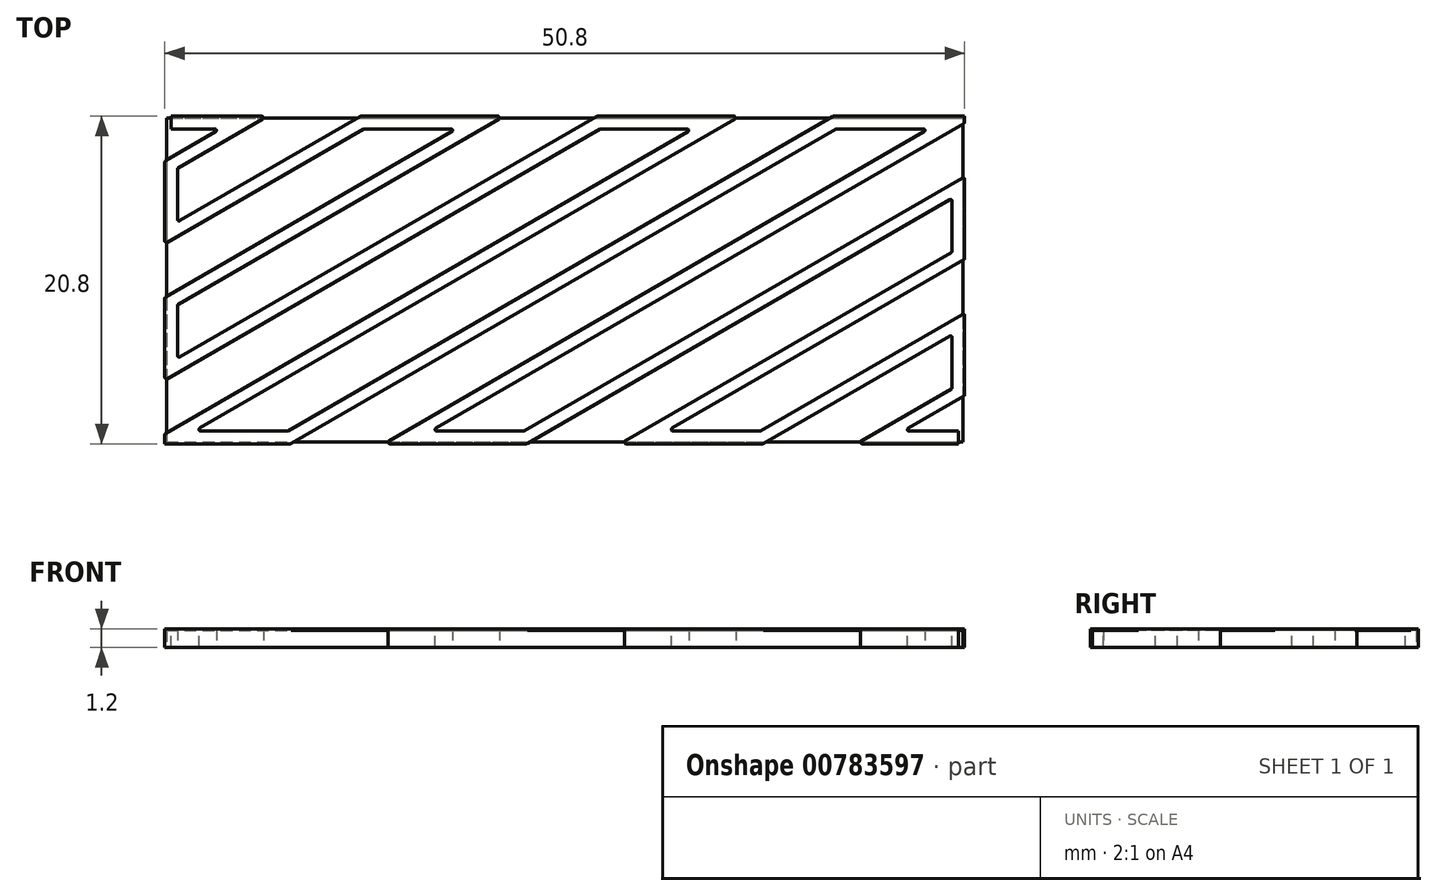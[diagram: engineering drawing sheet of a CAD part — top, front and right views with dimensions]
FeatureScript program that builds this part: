
annotation { "Feature Type Name" : "Feature", "Feature Type Description" : "" }
export const myFeature = defineFeature(function(context is Context, id is Id, definition is map)
    precondition{}
    {
        {
            var Q0;
            Q0=qCreatedBy(makeId("Top.planeOp"),FACE);
            var sketch = newSketch(context, id + "F0", { "sketchPlane" : qUnion([Q0])});
            skLineSegment(sketch, "E0.bottom", {"start": v(0, 0) * mm, "end": v(50, 0) * mm});
            skLineSegment(sketch, "E0.top", {"start": v(0, 20) * mm, "end": v(50, 20) * mm});
            skLineSegment(sketch, "E0.left", {"start": v(0, 0) * mm, "end": v(0, 20) * mm});
            skLineSegment(sketch, "E0.right", {"start": v(50, 0) * mm, "end": v(50, 20) * mm});
            skSolve(sketch);
        }
        {
            var Q0;
            Q0=qCreatedBy(makeId("Top.planeOp"),FACE);
            var sketch = newSketch(context, id + "F1", { "sketchPlane" : qUnion([Q0])});
            skLineSegment(sketch, "E1", {"start": v(0, 0) * mm, "end": v(34.64, 20) * mm});
            skLineSegment(sketch, "E2.1.0.0", {"start": v(7.5, 0) * mm, "end": v(42.14, 20) * mm});
            skLineSegment(sketch, "E2.2.0.0", {"start": v(15, 0) * mm, "end": v(49.64, 20) * mm});
            skLineSegment(sketch, "E2.3.0.0", {"start": v(22.5, 0) * mm, "end": v(50, 15.88) * mm});
            skLineSegment(sketch, "E2.4.0.0", {"start": v(30, 0) * mm, "end": v(50, 11.55) * mm});
            skLineSegment(sketch, "E2.5.0.0", {"start": v(37.5, 0) * mm, "end": v(50, 7.22) * mm});
            skLineSegment(sketch, "E2.6.0.0", {"start": v(45, 0) * mm, "end": v(50, 2.89) * mm});
            skLineSegment(sketch, "E3.1.0.0", {"start": v(0, 4.33) * mm, "end": v(27.14, 20) * mm});
            skLineSegment(sketch, "E3.2.0.0", {"start": v(0, 8.66) * mm, "end": v(19.64, 20) * mm});
            skLineSegment(sketch, "E3.3.0.0", {"start": v(0, 13) * mm, "end": v(12.14, 20) * mm});
            skLineSegment(sketch, "E3.4.0.0", {"start": v(0, 17.32) * mm, "end": v(4.64, 20) * mm});
            skLineSegment(sketch, "E4", {"start": v(0, 0) * mm, "end": v(7.5, 0) * mm});
            skLineSegment(sketch, "E5.1.0.0", {"start": v(15, 0) * mm, "end": v(22.5, 0) * mm});
            skLineSegment(sketch, "E5.2.0.0", {"start": v(30, 0) * mm, "end": v(37.5, 0) * mm});
            skLineSegment(sketch, "E5.3.0.0", {"start": v(45, 0) * mm, "end": v(50, 0) * mm});
            skLineSegment(sketch, "E6", {"start": v(0, 20) * mm, "end": v(4.64, 20) * mm});
            skLineSegment(sketch, "E7.1.0.0", {"start": v(12.14, 20) * mm, "end": v(19.64, 20) * mm});
            skLineSegment(sketch, "E7.2.0.0", {"start": v(27.14, 20) * mm, "end": v(34.64, 20) * mm});
            skLineSegment(sketch, "E7.3.0.0", {"start": v(42.14, 20) * mm, "end": v(49.64, 20) * mm});
            skPoint(sketch, "E8.orphan", {"position": v(-2.86, 20) * mm});
            skPoint(sketch, "E9.orphan", {"position": v(52.5, 0) * mm});
            skLineSegment(sketch, "E10", {"start": v(0, 4.33) * mm, "end": v(0, 8.66) * mm});
            skLineSegment(sketch, "E11", {"start": v(0, 13) * mm, "end": v(0, 17.32) * mm});
            skLineSegment(sketch, "E12", {"start": v(50, 15.88) * mm, "end": v(50, 11.55) * mm});
            skLineSegment(sketch, "E13", {"start": v(50, 7.22) * mm, "end": v(50, 2.89) * mm});
            skSolve(sketch);
        }
        {
            var Q0;
            Q0=sQuery(id+"F1.wireOp",VERTEX,"E6.start");
            var Q1;
            Q1=sQuery(id+"F1.wireOp",EDGE,"E6");
            cPlane(context, id + "F2", {"entities" : qUnion([Q0, Q1]), "cplaneType" : CPlaneType.LINE_POINT, "offset" : 25 * mm, "width" : 150 * mm, "height" : 150 * mm});
        }
        {
            var Q0;
            Q0=qCreatedBy(id+"F2.planeOp",FACE);
            var sketch = newSketch(context, id + "F3", { "sketchPlane" : qUnion([Q0])});
            skPoint(sketch, "E14.0", {"position": v(20, 0) * mm});
            skLineSegment(sketch, "E15", {"start": v(20, 0) * mm, "end": v(20.4, 0) * mm});
            skLineSegment(sketch, "E16", {"start": v(20.4, 0) * mm, "end": v(20.4, 1.2) * mm});
            skLineSegment(sketch, "E17", {"start": v(20.4, 1.2) * mm, "end": v(20, 1.2) * mm});
            skLineSegment(sketch, "E18", {"start": v(20, -0.76) * mm, "end": v(20, 2.5) * mm, "construction": true});
            skLineSegment(sketch, "E19.MirrorCS", {"start": v(19.6, 1.2) * mm, "end": v(20, 1.2) * mm});
            skLineSegment(sketch, "E20.MirrorCS", {"start": v(20, 0) * mm, "end": v(19.6, 0) * mm});
            skLineSegment(sketch, "E21.MirrorCS", {"start": v(19.6, 0) * mm, "end": v(19.6, 1.2) * mm});
            skSolve(sketch);
        }
        {
            var Q0;
            Q0 = qSketchRegion(id + "F3", true);
            var Q1;
            Q1=sQuery(id+"F1.wireOp",EDGE,"E6");
            var Q2;
            Q2=sQuery(id+"F1.wireOp",EDGE,"E3.4.0.0");
            var Q3;
            Q3=sQuery(id+"F1.wireOp",EDGE,"E11");
            var Q4;
            Q4=sQuery(id+"F1.wireOp",EDGE,"E3.3.0.0");
            var Q5;
            Q5=sQuery(id+"F1.wireOp",EDGE,"E7.1.0.0");
            var Q6;
            Q6=sQuery(id+"F1.wireOp",EDGE,"E3.2.0.0");
            var Q7;
            Q7=sQuery(id+"F1.wireOp",EDGE,"E10");
            var Q8;
            Q8=sQuery(id+"F1.wireOp",EDGE,"E3.1.0.0");
            var Q9;
            Q9=sQuery(id+"F1.wireOp",EDGE,"E7.2.0.0");
            var Q10;
            Q10=sQuery(id+"F1.wireOp",EDGE,"E1");
            var Q11;
            Q11=sQuery(id+"F1.wireOp",EDGE,"E4");
            var Q12;
            Q12=sQuery(id+"F1.wireOp",EDGE,"E2.1.0.0");
            var Q13;
            Q13=sQuery(id+"F1.wireOp",EDGE,"E2.2.0.0");
            var Q14;
            Q14=sQuery(id+"F1.wireOp",EDGE,"E7.3.0.0");
            var Q15;
            Q15=sQuery(id+"F1.wireOp",EDGE,"E5.1.0.0");
            var Q16;
            Q16=sQuery(id+"F1.wireOp",EDGE,"E2.3.0.0");
            var Q17;
            Q17=sQuery(id+"F1.wireOp",EDGE,"E12");
            var Q18;
            Q18=sQuery(id+"F1.wireOp",EDGE,"E2.4.0.0");
            var Q19;
            Q19=sQuery(id+"F1.wireOp",EDGE,"E5.2.0.0");
            var Q20;
            Q20=sQuery(id+"F1.wireOp",EDGE,"E2.5.0.0");
            var Q21;
            Q21=sQuery(id+"F1.wireOp",EDGE,"E13");
            var Q22;
            Q22=sQuery(id+"F1.wireOp",EDGE,"E2.6.0.0");
            var Q23;
            Q23=sQuery(id+"F1.wireOp",EDGE,"E5.3.0.0");
            sweep(context, id + "F4", {"profiles" : qUnion([Q0]), "path" : qUnion([Q1, Q2, Q3, Q4, Q5, Q6, Q7, Q8, Q9, Q10, Q11, Q12, Q13, Q14, Q15, Q16, Q17, Q18, Q19, Q20, Q21, Q22, Q23])});
        }
        {
            var Q0;
            Q0=qCreatedBy(makeId("Top.planeOp"),FACE);
            var sketch = newSketch(context, id + "F5", { "sketchPlane" : qUnion([Q0])});
            skLineSegment(sketch, "E22.0", {"start": v(-0.4, 8.9) * mm, "end": v(-0.4, 3.64) * mm});
            skLineSegment(sketch, "E23.0", {"start": v(0, 20.4) * mm, "end": v(6.13, 20.4) * mm});
            skLineSegment(sketch, "E24.0", {"start": v(28.5, -0.4) * mm, "end": v(37.6, -0.4) * mm});
            skLineSegment(sketch, "E25.0", {"start": v(50.4, 16.57) * mm, "end": v(50.4, 11.32) * mm});
            skLineSegment(sketch, "E26.bottom", {"start": v(-0.4, 20.4) * mm, "end": v(50.4, 20.4) * mm});
            skLineSegment(sketch, "E26.top", {"start": v(-0.4, -0.4) * mm, "end": v(50.4, -0.4) * mm});
            skLineSegment(sketch, "E26.left", {"start": v(-0.4, 20.4) * mm, "end": v(-0.4, -0.4) * mm});
            skLineSegment(sketch, "E26.right", {"start": v(50.4, 20.4) * mm, "end": v(50.4, -0.4) * mm});
            skLineSegment(sketch, "E27.bottom", {"start": v(-6.4, 28.18) * mm, "end": v(56.43, 28.18) * mm});
            skLineSegment(sketch, "E27.top", {"start": v(-6.4, -9.1) * mm, "end": v(56.43, -9.1) * mm});
            skLineSegment(sketch, "E27.left", {"start": v(-6.4, 28.18) * mm, "end": v(-6.4, -9.1) * mm});
            skLineSegment(sketch, "E27.right", {"start": v(56.43, 28.18) * mm, "end": v(56.43, -9.1) * mm});
            skSolve(sketch);
        }
        {
            var Q0;
            {var subQ1=sQuery(id+"F5.wireOp",EDGE,"E22.0");Q0=makeQuery(id+"F5.imprint","IMPRINT",FACE,{"disambiguationData":[TD([[makeQuery(id+"F5.imprint","IMPRINT",EDGE,{"derivedFrom":subQ1}),-1.0]])]});}
            extrude(context, id + "F6", {"entities" : qUnion([Q0]), "depth" : 25 * mm, "offsetDistance" : 25 * mm});
        }
        {
            var Q0;
            Q0=makeQuery(id+"F6.opExtrude","SWEPT_BODY",BODY,{"disambiguationData":[OSD([sQuery(id+"F5.wireOp",EDGE,"E22.0"),sQuery(id+"F5.wireOp",EDGE,"E23.0"),sQuery(id+"F5.wireOp",EDGE,"E24.0"),sQuery(id+"F5.wireOp",EDGE,"E25.0"),sQuery(id+"F5.wireOp",EDGE,"E26.bottom"),sQuery(id+"F5.wireOp",EDGE,"E26.top"),sQuery(id+"F5.wireOp",EDGE,"E26.left"),sQuery(id+"F5.wireOp",EDGE,"E26.right"),sQuery(id+"F5.wireOp",EDGE,"E27.bottom"),sQuery(id+"F5.wireOp",EDGE,"E27.top"),sQuery(id+"F5.wireOp",EDGE,"E27.left"),sQuery(id+"F5.wireOp",EDGE,"E27.right")])]});
            var Q1;
            Q1=makeQuery(id+"F4.opSweep","SWEPT_BODY",BODY,{"disambiguationData":[OSD([sQuery(id+"F1.wireOp",EDGE,"E2.1.0.0"),sQuery(id+"F3.wireOp",EDGE,"E15"),sQuery(id+"F3.wireOp",EDGE,"E16"),sQuery(id+"F3.wireOp",EDGE,"E17"),sQuery(id+"F3.wireOp",EDGE,"E19.MirrorCS"),sQuery(id+"F3.wireOp",EDGE,"E20.MirrorCS"),sQuery(id+"F3.wireOp",EDGE,"E21.MirrorCS")])]});
            booleanBodies(context, id + "F7", {"operationType" : BooleanOperationType.SUBTRACTION, "tools" : qUnion([Q0]), "targets" : qUnion([Q1])});
        }
        {
            var Q0;
            Q0=qCreatedBy(makeId("Top.planeOp"),FACE);
            var sketch = newSketch(context, id + "F8", { "sketchPlane" : qUnion([Q0])});
            skLineSegment(sketch, "E28.0", {"start": v(-0.3, 20.3) * mm, "end": v(50.3, 20.3) * mm});
            skLineSegment(sketch, "E28.1", {"start": v(-0.3, 20.3) * mm, "end": v(-0.3, -0.3) * mm});
            skLineSegment(sketch, "E28.2", {"start": v(-0.3, -0.3) * mm, "end": v(50.3, -0.3) * mm});
            skLineSegment(sketch, "E28.3", {"start": v(50.3, 20.3) * mm, "end": v(50.3, -0.3) * mm});
            skSolve(sketch);
        }
        {
            var Q0;
            Q0 = qSketchRegion(id + "F8", true);
            extrude(context, id + "F9", {"entities" : qUnion([Q0]), "depth" : 1.1 * mm, "offsetDistance" : 25 * mm});
        }
        {
            var Q0;
            Q0=makeQuery(id+"F4.opSweep","MID_CAP_EDGE",EDGE,{"disambiguationData":[OSD([sQuery(id+"F1.wireOp",VERTEX,"E11.end"),sQuery(id+"F3.wireOp",EDGE,"E21.MirrorCS")])],"capPos":2.0});
            var Q1;
            Q1=makeQuery(id+"F4.opSweep","MID_CAP_EDGE",EDGE,{"disambiguationData":[OSD([sQuery(id+"F1.wireOp",VERTEX,"E3.4.0.0.end"),sQuery(id+"F3.wireOp",EDGE,"E21.MirrorCS")])],"capPos":1.0});
            var Q2;
            Q2=makeQuery(id+"F4.opSweep","MID_CAP_EDGE",EDGE,{"disambiguationData":[OSD([sQuery(id+"F1.wireOp",VERTEX,"E3.4.0.0.end"),sQuery(id+"F3.wireOp",EDGE,"E16")])],"capPos":1.0});
            var Q3;
            Q3=makeQuery(id+"F4.opSweep","MID_CAP_EDGE",EDGE,{"disambiguationData":[OSD([sQuery(id+"F1.wireOp",VERTEX,"E11.end"),sQuery(id+"F3.wireOp",EDGE,"E16")])],"capPos":2.0});
            var Q4;
            Q4=makeQuery(id+"F4.opSweep","MID_CAP_EDGE",EDGE,{"disambiguationData":[OSD([sQuery(id+"F1.wireOp",VERTEX,"E3.3.0.0.start"),sQuery(id+"F3.wireOp",EDGE,"E16")])],"capPos":3.0});
            var Q5;
            Q5=makeQuery(id+"F4.opSweep","MID_CAP_EDGE",EDGE,{"disambiguationData":[OSD([sQuery(id+"F1.wireOp",VERTEX,"E3.3.0.0.start"),sQuery(id+"F3.wireOp",EDGE,"E21.MirrorCS")])],"capPos":3.0});
            var Q6;
            Q6=makeQuery(id+"F4.opSweep","MID_CAP_EDGE",EDGE,{"disambiguationData":[OSD([sQuery(id+"F1.wireOp",VERTEX,"E7.1.0.0.start"),sQuery(id+"F3.wireOp",EDGE,"E21.MirrorCS")])],"capPos":4.0});
            var Q7;
            Q7=makeQuery(id+"F4.opSweep","MID_CAP_EDGE",EDGE,{"disambiguationData":[OSD([sQuery(id+"F1.wireOp",VERTEX,"E7.1.0.0.start"),sQuery(id+"F3.wireOp",EDGE,"E16")])],"capPos":4.0});
            var Q8;
            Q8=makeQuery(id+"F4.opSweep","MID_CAP_EDGE",EDGE,{"disambiguationData":[OSD([sQuery(id+"F1.wireOp",VERTEX,"E3.2.0.0.end"),sQuery(id+"F3.wireOp",EDGE,"E21.MirrorCS")])],"capPos":5.0});
            var Q9;
            Q9=makeQuery(id+"F4.opSweep","MID_CAP_EDGE",EDGE,{"disambiguationData":[OSD([sQuery(id+"F1.wireOp",VERTEX,"E3.2.0.0.end"),sQuery(id+"F3.wireOp",EDGE,"E16")])],"capPos":5.0});
            var Q10;
            Q10=makeQuery(id+"F4.opSweep","MID_CAP_EDGE",EDGE,{"disambiguationData":[OSD([sQuery(id+"F1.wireOp",VERTEX,"E7.2.0.0.start"),sQuery(id+"F3.wireOp",EDGE,"E16")])],"capPos":8.0});
            var Q11;
            Q11=makeQuery(id+"F4.opSweep","MID_CAP_EDGE",EDGE,{"disambiguationData":[OSD([sQuery(id+"F1.wireOp",VERTEX,"E10.end"),sQuery(id+"F3.wireOp",EDGE,"E21.MirrorCS")])],"capPos":6.0});
            var Q12;
            Q12=makeQuery(id+"F4.opSweep","MID_CAP_EDGE",EDGE,{"disambiguationData":[OSD([sQuery(id+"F1.wireOp",VERTEX,"E10.end"),sQuery(id+"F3.wireOp",EDGE,"E16")])],"capPos":6.0});
            var Q13;
            Q13=makeQuery(id+"F4.opSweep","MID_CAP_EDGE",EDGE,{"disambiguationData":[OSD([sQuery(id+"F1.wireOp",VERTEX,"E3.1.0.0.start"),sQuery(id+"F3.wireOp",EDGE,"E16")])],"capPos":7.0});
            var Q14;
            Q14=makeQuery(id+"F4.opSweep","MID_CAP_EDGE",EDGE,{"disambiguationData":[OSD([sQuery(id+"F1.wireOp",VERTEX,"E3.1.0.0.start"),sQuery(id+"F3.wireOp",EDGE,"E21.MirrorCS")])],"capPos":7.0});
            var Q15;
            Q15=makeQuery(id+"F4.opSweep","MID_CAP_EDGE",EDGE,{"disambiguationData":[OSD([sQuery(id+"F1.wireOp",VERTEX,"E7.2.0.0.start"),sQuery(id+"F3.wireOp",EDGE,"E21.MirrorCS")])],"capPos":8.0});
            var Q16;
            Q16=makeQuery(id+"F4.opSweep","MID_CAP_EDGE",EDGE,{"disambiguationData":[OSD([sQuery(id+"F1.wireOp",VERTEX,"E1.end"),sQuery(id+"F3.wireOp",EDGE,"E21.MirrorCS")])],"capPos":9.0});
            var Q17;
            Q17=makeQuery(id+"F4.opSweep","MID_CAP_EDGE",EDGE,{"disambiguationData":[OSD([sQuery(id+"F1.wireOp",VERTEX,"E1.end"),sQuery(id+"F3.wireOp",EDGE,"E16")])],"capPos":9.0});
            var Q18;
            Q18=makeQuery(id+"F4.opSweep","MID_CAP_EDGE",EDGE,{"disambiguationData":[OSD([sQuery(id+"F1.wireOp",VERTEX,"E7.3.0.0.start"),sQuery(id+"F3.wireOp",EDGE,"E16")])],"capPos":12.0});
            var Q19;
            Q19=makeQuery(id+"F7.opBoolean","INTERSECT",EDGE,{"derivedFrom":[makeQuery(id+"F4.opSweep","SWEPT_FACE",FACE,{"disambiguationData":[OSD([sQuery(id+"F1.wireOp",EDGE,"E1"),sQuery(id+"F3.wireOp",EDGE,"E21.MirrorCS")])]}),makeQuery(id+"F6.opExtrude","SWEPT_FACE",FACE,{"disambiguationData":[OSD([sQuery(id+"F5.wireOp",EDGE,"E22.0"),sQuery(id+"F5.wireOp",EDGE,"E26.left")])]})]});
            var Q20;
            Q20=makeQuery(id+"F4.opSweep","MID_CAP_EDGE",EDGE,{"disambiguationData":[OSD([sQuery(id+"F1.wireOp",VERTEX,"E4.start"),sQuery(id+"F3.wireOp",EDGE,"E16")])],"capPos":10.0});
            var Q21;
            Q21=makeQuery(id+"F7.opBoolean","COPY",EDGE,{"derivedFrom":makeQuery(id+"F6.opExtrude","SWEPT_EDGE",EDGE,{"disambiguationData":[OSD([sQuery(id+"F5.wireOp",EDGE,"E26.top"),sQuery(id+"F5.wireOp",EDGE,"E26.left")])]})});
            var Q22;
            Q22=makeQuery(id+"F4.opSweep","MID_CAP_EDGE",EDGE,{"disambiguationData":[OSD([sQuery(id+"F1.wireOp",VERTEX,"E2.1.0.0.start"),sQuery(id+"F3.wireOp",EDGE,"E16")])],"capPos":11.0});
            var Q23;
            Q23=makeQuery(id+"F4.opSweep","MID_CAP_EDGE",EDGE,{"disambiguationData":[OSD([sQuery(id+"F1.wireOp",VERTEX,"E2.1.0.0.start"),sQuery(id+"F3.wireOp",EDGE,"E21.MirrorCS")])],"capPos":11.0});
            var Q24;
            Q24=makeQuery(id+"F4.opSweep","MID_CAP_EDGE",EDGE,{"disambiguationData":[OSD([sQuery(id+"F1.wireOp",VERTEX,"E7.3.0.0.start"),sQuery(id+"F3.wireOp",EDGE,"E21.MirrorCS")])],"capPos":12.0});
            var Q25;
            Q25=makeQuery(id+"F4.opSweep","MID_CAP_EDGE",EDGE,{"disambiguationData":[OSD([sQuery(id+"F1.wireOp",VERTEX,"E7.3.0.0.end"),sQuery(id+"F3.wireOp",EDGE,"E21.MirrorCS")])],"capPos":13.0});
            var Q26;
            Q26=makeQuery(id+"F7.opBoolean","COPY",EDGE,{"derivedFrom":makeQuery(id+"F6.opExtrude","SWEPT_EDGE",EDGE,{"disambiguationData":[OSD([sQuery(id+"F5.wireOp",EDGE,"E26.bottom"),sQuery(id+"F5.wireOp",EDGE,"E26.right")])]})});
            var Q27;
            Q27=makeQuery(id+"F7.opBoolean","INTERSECT",EDGE,{"derivedFrom":[makeQuery(id+"F4.opSweep","SWEPT_FACE",FACE,{"disambiguationData":[OSD([sQuery(id+"F1.wireOp",EDGE,"E2.2.0.0"),sQuery(id+"F3.wireOp",EDGE,"E16")])]}),makeQuery(id+"F6.opExtrude","SWEPT_FACE",FACE,{"disambiguationData":[OSD([sQuery(id+"F5.wireOp",EDGE,"E25.0"),sQuery(id+"F5.wireOp",EDGE,"E26.right")])]})]});
            var Q28;
            Q28=makeQuery(id+"F4.opSweep","MID_CAP_EDGE",EDGE,{"disambiguationData":[OSD([sQuery(id+"F1.wireOp",VERTEX,"E12.start"),sQuery(id+"F3.wireOp",EDGE,"E16")])],"capPos":16.0});
            var Q29;
            Q29=makeQuery(id+"F4.opSweep","MID_CAP_EDGE",EDGE,{"disambiguationData":[OSD([sQuery(id+"F1.wireOp",VERTEX,"E12.start"),sQuery(id+"F3.wireOp",EDGE,"E21.MirrorCS")])],"capPos":16.0});
            var Q30;
            Q30=makeQuery(id+"F4.opSweep","MID_CAP_EDGE",EDGE,{"disambiguationData":[OSD([sQuery(id+"F1.wireOp",VERTEX,"E2.4.0.0.end"),sQuery(id+"F3.wireOp",EDGE,"E21.MirrorCS")])],"capPos":17.0});
            var Q31;
            Q31=makeQuery(id+"F4.opSweep","MID_CAP_EDGE",EDGE,{"disambiguationData":[OSD([sQuery(id+"F1.wireOp",VERTEX,"E2.4.0.0.end"),sQuery(id+"F3.wireOp",EDGE,"E16")])],"capPos":17.0});
            var Q32;
            Q32=makeQuery(id+"F4.opSweep","MID_CAP_EDGE",EDGE,{"disambiguationData":[OSD([sQuery(id+"F1.wireOp",VERTEX,"E5.2.0.0.start"),sQuery(id+"F3.wireOp",EDGE,"E21.MirrorCS")])],"capPos":18.0});
            var Q33;
            Q33=makeQuery(id+"F4.opSweep","MID_CAP_EDGE",EDGE,{"disambiguationData":[OSD([sQuery(id+"F1.wireOp",VERTEX,"E5.2.0.0.start"),sQuery(id+"F3.wireOp",EDGE,"E16")])],"capPos":18.0});
            var Q34;
            Q34=makeQuery(id+"F4.opSweep","MID_CAP_EDGE",EDGE,{"disambiguationData":[OSD([sQuery(id+"F1.wireOp",VERTEX,"E2.3.0.0.start"),sQuery(id+"F3.wireOp",EDGE,"E21.MirrorCS")])],"capPos":15.0});
            var Q35;
            Q35=makeQuery(id+"F4.opSweep","MID_CAP_EDGE",EDGE,{"disambiguationData":[OSD([sQuery(id+"F1.wireOp",VERTEX,"E5.1.0.0.start"),sQuery(id+"F3.wireOp",EDGE,"E21.MirrorCS")])],"capPos":14.0});
            var Q36;
            Q36=makeQuery(id+"F4.opSweep","MID_CAP_EDGE",EDGE,{"disambiguationData":[OSD([sQuery(id+"F1.wireOp",VERTEX,"E5.1.0.0.start"),sQuery(id+"F3.wireOp",EDGE,"E16")])],"capPos":14.0});
            var Q37;
            Q37=makeQuery(id+"F4.opSweep","MID_CAP_EDGE",EDGE,{"disambiguationData":[OSD([sQuery(id+"F1.wireOp",VERTEX,"E2.5.0.0.start"),sQuery(id+"F3.wireOp",EDGE,"E16")])],"capPos":19.0});
            var Q38;
            Q38=makeQuery(id+"F4.opSweep","MID_CAP_EDGE",EDGE,{"disambiguationData":[OSD([sQuery(id+"F1.wireOp",VERTEX,"E2.3.0.0.start"),sQuery(id+"F3.wireOp",EDGE,"E16")])],"capPos":15.0});
            var Q39;
            Q39=makeQuery(id+"F4.opSweep","MID_CAP_EDGE",EDGE,{"disambiguationData":[OSD([sQuery(id+"F1.wireOp",VERTEX,"E13.start"),sQuery(id+"F3.wireOp",EDGE,"E16")])],"capPos":20.0});
            var Q40;
            Q40=makeQuery(id+"F4.opSweep","MID_CAP_EDGE",EDGE,{"disambiguationData":[OSD([sQuery(id+"F1.wireOp",VERTEX,"E13.start"),sQuery(id+"F3.wireOp",EDGE,"E21.MirrorCS")])],"capPos":20.0});
            var Q41;
            Q41=makeQuery(id+"F4.opSweep","MID_CAP_EDGE",EDGE,{"disambiguationData":[OSD([sQuery(id+"F1.wireOp",VERTEX,"E2.5.0.0.start"),sQuery(id+"F3.wireOp",EDGE,"E21.MirrorCS")])],"capPos":19.0});
            var Q42;
            Q42=makeQuery(id+"F4.opSweep","MID_CAP_EDGE",EDGE,{"disambiguationData":[OSD([sQuery(id+"F1.wireOp",VERTEX,"E5.3.0.0.start"),sQuery(id+"F3.wireOp",EDGE,"E21.MirrorCS")])],"capPos":22.0});
            var Q43;
            Q43=makeQuery(id+"F4.opSweep","MID_CAP_EDGE",EDGE,{"disambiguationData":[OSD([sQuery(id+"F1.wireOp",VERTEX,"E2.6.0.0.end"),sQuery(id+"F3.wireOp",EDGE,"E16")])],"capPos":21.0});
            var Q44;
            Q44=makeQuery(id+"F4.opSweep","MID_CAP_EDGE",EDGE,{"disambiguationData":[OSD([sQuery(id+"F1.wireOp",VERTEX,"E5.3.0.0.start"),sQuery(id+"F3.wireOp",EDGE,"E16")])],"capPos":22.0});
            var Q45;
            Q45=makeQuery(id+"F4.opSweep","MID_CAP_EDGE",EDGE,{"disambiguationData":[OSD([sQuery(id+"F1.wireOp",VERTEX,"E2.6.0.0.end"),sQuery(id+"F3.wireOp",EDGE,"E21.MirrorCS")])],"capPos":21.0});
            fillet(context, id + "F10", {"entities" : qUnion([Q0, Q1, Q2, Q3, Q4, Q5, Q6, Q7, Q8, Q9, Q10, Q11, Q12, Q13, Q14, Q15, Q16, Q17, Q18, Q19, Q20, Q21, Q22, Q23, Q24, Q25, Q26, Q27, Q28, Q29, Q30, Q31, Q32, Q33, Q34, Q35, Q36, Q37, Q38, Q39, Q40, Q41, Q42, Q43, Q44, Q45]), "radius" : .1 * mm, "tangentPropagation" : true, "allowEdgeOverflow" : false});
        }
    });
